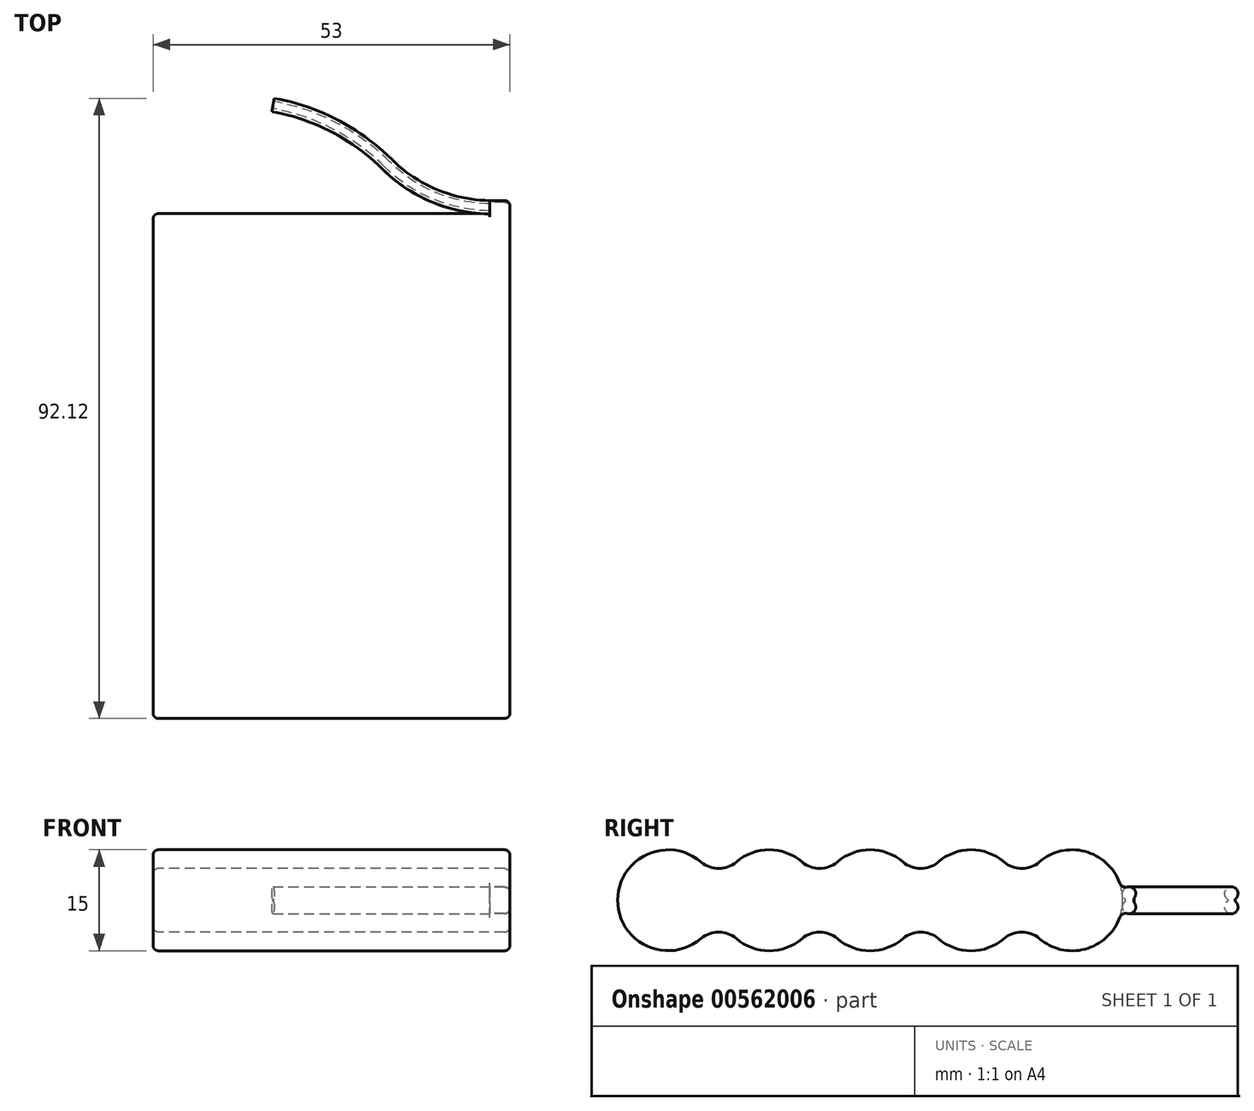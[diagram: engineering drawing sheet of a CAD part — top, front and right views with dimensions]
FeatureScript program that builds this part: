
annotation { "Feature Type Name" : "Feature", "Feature Type Description" : "" }
export const myFeature = defineFeature(function(context is Context, id is Id, definition is map)
    precondition{}
    {
        {
            var Q0;
            Q0=qCreatedBy(makeId("Right.planeOp"),FACE);
            var sketch = newSketch(context, id + "F0", { "sketchPlane" : qUnion([Q0])});
            skArc(sketch, "E0", {"start": v(12.4, 5.69) * mm, "mid": v(0, 0) * mm, "end": v(12.4, -5.69) * mm});
            skArc(sketch, "E1", {"start": v(17.6, -5.69) * mm, "mid": v(22.5, -7.5) * mm, "end": v(27.4, -5.69) * mm});
            skArc(sketch, "E2", {"start": v(32.6, -5.69) * mm, "mid": v(37.5, -7.5) * mm, "end": v(42.4, -5.69) * mm});
            skArc(sketch, "E3", {"start": v(47.6, -5.69) * mm, "mid": v(52.5, -7.5) * mm, "end": v(57.4, -5.69) * mm});
            skArc(sketch, "E4", {"start": v(62.6, -5.69) * mm, "mid": v(69.38, -7.26) * mm, "end": v(74.54, -2.6) * mm});
            skArc(sketch, "E5", {"start": v(12.4, 5.69) * mm, "mid": v(15, 4.72) * mm, "end": v(17.6, 5.69) * mm});
            skArc(sketch, "E6", {"start": v(27.4, 5.69) * mm, "mid": v(30, 4.72) * mm, "end": v(32.6, 5.69) * mm});
            skArc(sketch, "E7", {"start": v(42.4, 5.69) * mm, "mid": v(45, 4.72) * mm, "end": v(47.6, 5.69) * mm});
            skArc(sketch, "E8", {"start": v(57.4, 5.69) * mm, "mid": v(60, 4.72) * mm, "end": v(62.6, 5.69) * mm});
            skArc(sketch, "E9", {"start": v(62.6, -5.69) * mm, "mid": v(60, -4.72) * mm, "end": v(57.4, -5.69) * mm});
            skArc(sketch, "E10", {"start": v(47.6, -5.69) * mm, "mid": v(45, -4.72) * mm, "end": v(42.4, -5.69) * mm});
            skArc(sketch, "E11", {"start": v(32.6, -5.69) * mm, "mid": v(30, -4.72) * mm, "end": v(27.4, -5.69) * mm});
            skArc(sketch, "E12", {"start": v(17.6, -5.69) * mm, "mid": v(15, -4.72) * mm, "end": v(12.4, -5.69) * mm});
            skArc(sketch, "E13.trimOffspring", {"start": v(27.4, 5.69) * mm, "mid": v(22.5, 7.5) * mm, "end": v(17.6, 5.69) * mm});
            skArc(sketch, "E14.trimOffspring", {"start": v(42.4, 5.69) * mm, "mid": v(37.5, 7.5) * mm, "end": v(32.6, 5.69) * mm});
            skArc(sketch, "E15.trimOffspring", {"start": v(57.4, 5.69) * mm, "mid": v(52.5, 7.5) * mm, "end": v(47.6, 5.69) * mm});
            skArc(sketch, "E16", {"start": v(76.8, 0.5) * mm, "mid": v(76.74, 1.6) * mm, "end": v(75.7, 1.97) * mm});
            skArc(sketch, "E17", {"start": v(75.7, -1.97) * mm, "mid": v(76.74, -1.6) * mm, "end": v(76.8, -0.5) * mm});
            skArc(sketch, "E18.trimOffspring", {"start": v(74.54, 2.6) * mm, "mid": v(69.38, 7.26) * mm, "end": v(62.6, 5.69) * mm});
            skPoint(sketch, "E19.visualSharp", {"position": v(74.95, 0.88) * mm});
            skArc(sketch, "E19.filletArc", {"start": v(74.54, 2.6) * mm, "mid": v(75, 2.06) * mm, "end": v(75.7, 1.97) * mm});
            skPoint(sketch, "E20.visualSharp", {"position": v(74.95, -0.88) * mm});
            skArc(sketch, "E20.filletArc", {"start": v(75.7, -1.97) * mm, "mid": v(75, -2.06) * mm, "end": v(74.54, -2.6) * mm});
            skPoint(sketch, "E21.visualSharp", {"position": v(75.94, 0) * mm});
            skArc(sketch, "E21.filletArc", {"start": v(76.8, 0.5) * mm, "mid": v(76.67, 0) * mm, "end": v(76.8, -0.5) * mm});
            skSolve(sketch);
        }
        {
            var Q0;
            Q0 = qSketchRegion(id + "F0", true);
            extrude(context, id + "F1", {"entities" : qUnion([Q0]), "depth" : 53 * mm, "offsetDistance" : 25 * mm});
        }
        {
            var Q0;
            Q0=makeQuery(id+"F1.opExtrude","CAP_FACE",FACE,{"disambiguationData":[OSD([sQuery(id+"F0.wireOp",EDGE,"E0"),sQuery(id+"F0.wireOp",EDGE,"E1"),sQuery(id+"F0.wireOp",EDGE,"E2"),sQuery(id+"F0.wireOp",EDGE,"E3"),sQuery(id+"F0.wireOp",EDGE,"E4"),sQuery(id+"F0.wireOp",EDGE,"E5"),sQuery(id+"F0.wireOp",EDGE,"E6"),sQuery(id+"F0.wireOp",EDGE,"E7"),sQuery(id+"F0.wireOp",EDGE,"E8"),sQuery(id+"F0.wireOp",EDGE,"E9"),sQuery(id+"F0.wireOp",EDGE,"E10"),sQuery(id+"F0.wireOp",EDGE,"E11"),sQuery(id+"F0.wireOp",EDGE,"E12"),sQuery(id+"F0.wireOp",EDGE,"E13.trimOffspring"),sQuery(id+"F0.wireOp",EDGE,"E14.trimOffspring"),sQuery(id+"F0.wireOp",EDGE,"E15.trimOffspring"),sQuery(id+"F0.wireOp",EDGE,"E16"),sQuery(id+"F0.wireOp",EDGE,"E17"),sQuery(id+"F0.wireOp",EDGE,"E18.trimOffspring")])],"isStart":true});
            var sketch = newSketch(context, id + "F2", { "sketchPlane" : qUnion([Q0])});
            skArc(sketch, "E22", {"start": v(-74.13, 3.5) * mm, "mid": v(-75, 0.22) * mm, "end": v(-74.32, -3.11) * mm});
            skArc(sketch, "E23", {"start": v(-76.35, 4.68) * mm, "mid": v(-77.5, 0.29) * mm, "end": v(-76.6, -4.16) * mm});
            skLineSegment(sketch, "E24", {"start": v(-74.13, 3.5) * mm, "end": v(-76.35, 4.68) * mm});
            skLineSegment(sketch, "E25", {"start": v(-74.32, -3.11) * mm, "end": v(-76.6, -4.16) * mm});
            skSolve(sketch);
        }
        {
            var Q0;
            Q0 = qSketchRegion(id + "F2", true);
            extrude(context, id + "F3", {"entities" : qUnion([Q0]), "operationType" : NewBodyOperationType.REMOVE, "oppositeDirection" : true, "depth" : 50 * mm, "offsetDistance" : 25 * mm});
        }
        {
            var Q0;
            Q0=makeQuery(id+"F3.boolean.opBoolean","COPY",FACE,{"derivedFrom":makeQuery(id+"F3.opExtrude","CAP_FACE",FACE,{"disambiguationData":[OSD([sQuery(id+"F2.wireOp",EDGE,"E22"),sQuery(id+"F2.wireOp",EDGE,"E23"),sQuery(id+"F2.wireOp",EDGE,"E24"),sQuery(id+"F2.wireOp",EDGE,"E25")])],"isStart":false})});
            var sketch = newSketch(context, id + "F4", { "sketchPlane" : qUnion([Q0])});
            skArc(sketch, "E26", {"start": v(-75.3, 0.23) * mm, "mid": v(-75.94, 2) * mm, "end": v(-76.58, 0.23) * mm});
            skArc(sketch, "E27", {"start": v(-76.58, -0.23) * mm, "mid": v(-75.94, -2) * mm, "end": v(-75.3, -0.23) * mm});
            skArc(sketch, "E28", {"start": v(-76.58, -0.23) * mm, "mid": v(-76.47, 0) * mm, "end": v(-76.58, 0.23) * mm});
            skArc(sketch, "E29", {"start": v(-75.3, 0.23) * mm, "mid": v(-75.41, 0) * mm, "end": v(-75.3, -0.23) * mm});
            skSolve(sketch);
        }
        {
            var Q0;
            Q0=qCreatedBy(makeId("Top.planeOp"),FACE);
            var sketch = newSketch(context, id + "F5", { "sketchPlane" : qUnion([Q0])});
            skArc(sketch, "E30", {"start": v(34.76, 82.33) * mm, "mid": v(41.76, 77.65) * mm, "end": v(50, 75.94) * mm});
            skArc(sketch, "E31", {"start": v(34.76, 82.33) * mm, "mid": v(26.96, 88.02) * mm, "end": v(17.82, 91.13) * mm});
            skSolve(sketch);
        }
        {
            var Q0;
            Q0 = qSketchRegion(id + "F4", true);
            var Q1;
            Q1 = qConstructionFilter(qBodyType(qCreatedBy(id + "F5" ,EDGE), BodyType.WIRE), ConstructionObject.NO);
            sweep(context, id + "F6", {"profiles" : qUnion([Q0]), "path" : qUnion([Q1])});
        }
        {
            var Q0;
            Q0=makeQuery(id+"F1.opExtrude","CAP_EDGE",EDGE,{"disambiguationData":[OSD([sQuery(id+"F0.wireOp",EDGE,"E0")])],"isStart":true});
            var Q1;
            Q1=makeQuery(id+"F1.opExtrude","CAP_EDGE",EDGE,{"disambiguationData":[OSD([sQuery(id+"F0.wireOp",EDGE,"E15.trimOffspring")])],"isStart":false});
            fillet(context, id + "F7", {"entities" : qUnion([Q0, Q1]), "radius" : 0.8 * mm, "tangentPropagation" : true, "allowEdgeOverflow" : false});
        }
    });
